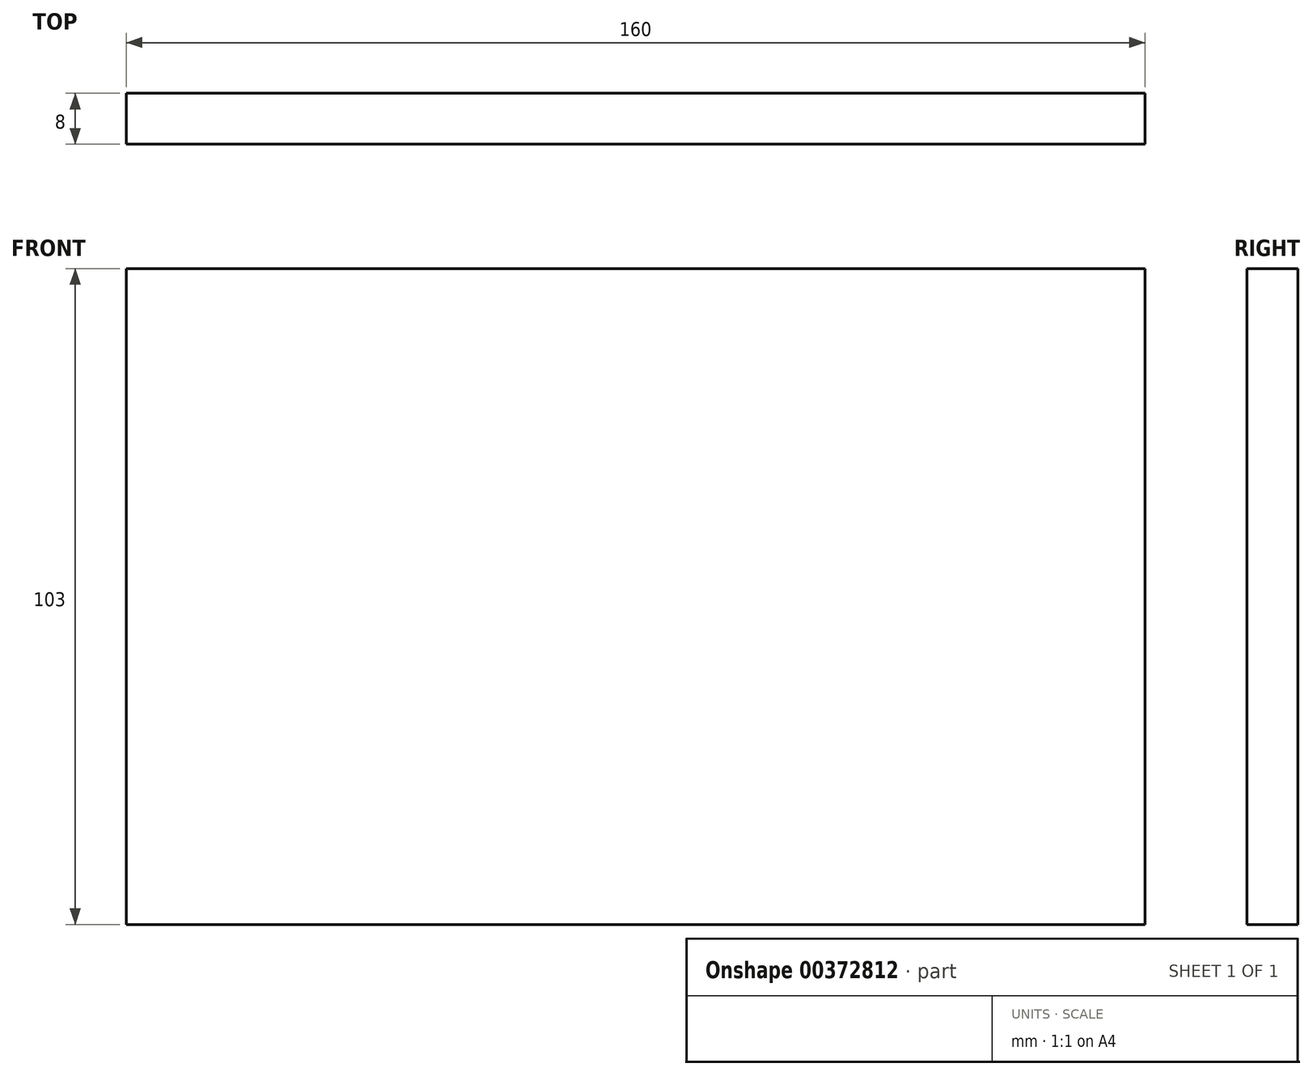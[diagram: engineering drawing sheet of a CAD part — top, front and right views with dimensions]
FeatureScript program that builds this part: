
annotation { "Feature Type Name" : "Feature", "Feature Type Description" : "" }
export const myFeature = defineFeature(function(context is Context, id is Id, definition is map)
    precondition{}
    {
        {
            var Q0;
            Q0=qCreatedBy(makeId("Front.planeOp"),FACE);
            var sketch = newSketch(context, id + "F0", { "sketchPlane" : qUnion([Q0])});
            skLineSegment(sketch, "E0.bottom", {"start": v(80, -51.5) * mm, "end": v(-80, -51.5) * mm});
            skLineSegment(sketch, "E0.top", {"start": v(80, 51.5) * mm, "end": v(-80, 51.5) * mm});
            skLineSegment(sketch, "E0.left", {"start": v(80, -51.5) * mm, "end": v(80, 51.5) * mm});
            skLineSegment(sketch, "E0.right", {"start": v(-80, -51.5) * mm, "end": v(-80, 51.5) * mm});
            skPoint(sketch, "E0.middle", {"position": v(0, 0) * mm});
            skSolve(sketch);
        }
        {
            var Q0;
            Q0=makeQuery(id+"F0.imprint","IMPRINT",FACE,{"disambiguationData":[TD([[makeQuery(id+"F0.imprint","IMPRINT",EDGE,{"derivedFrom":sQuery(id+"F0.wireOp",EDGE,"E0.bottom")}),-1.0]])]});
            extrude(context, id + "F1", {"entities" : qUnion([Q0]), "endBound" : BoundingType.SYMMETRIC, "depth" : 8 * mm});
        }
    });
